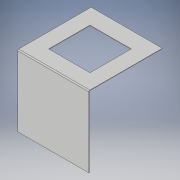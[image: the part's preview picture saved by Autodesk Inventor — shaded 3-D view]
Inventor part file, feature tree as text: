
AUTODESK INVENTOR PART (.ipt)
format: ipt  version: 2019 (Build 230136000, 136)  size: 123,392 bytes
history: native  units: in
note: dims shown in document units (in); Inventor stores cm internally (conversion verified against a paired STEP export)
features: sheet_metal_op x4, sketch x3, other x2, extrude x1
ambient origin geometry x8: Origin, YZ Plane, XZ Plane, XY Plane, X Axis, Y Axis, Z Axis, Center Point
bodies: Solid1 (feature_tree)
feature tree (10):
  sheet_metal_op  "Face1"
  sheet_metal_op  "Flange1"
  extrude  "Extrusion1"  Depth=4.0in
  sketch  "Sketch1"  dims[d0=3.875in d1=4.0in]
  other  "Plate1"
  sketch  "Sketch2"  dims[d2=0.0281in]
  other  "Plate2"
  sheet_metal_op  "Bend1"
  sheet_metal_op  "Corner1"
  sketch  "Sketch3"  dims[d3=0.0281in d4=0.0141in d5=0.0563in d6=0.0281in d7=3.875in d8=90.0deg d9=0.0281in d10=0.1125in d11=0.0281in d12=0.0281in d13=2.25in d14=2.25in d15=0.0281in d16=0.0in]
